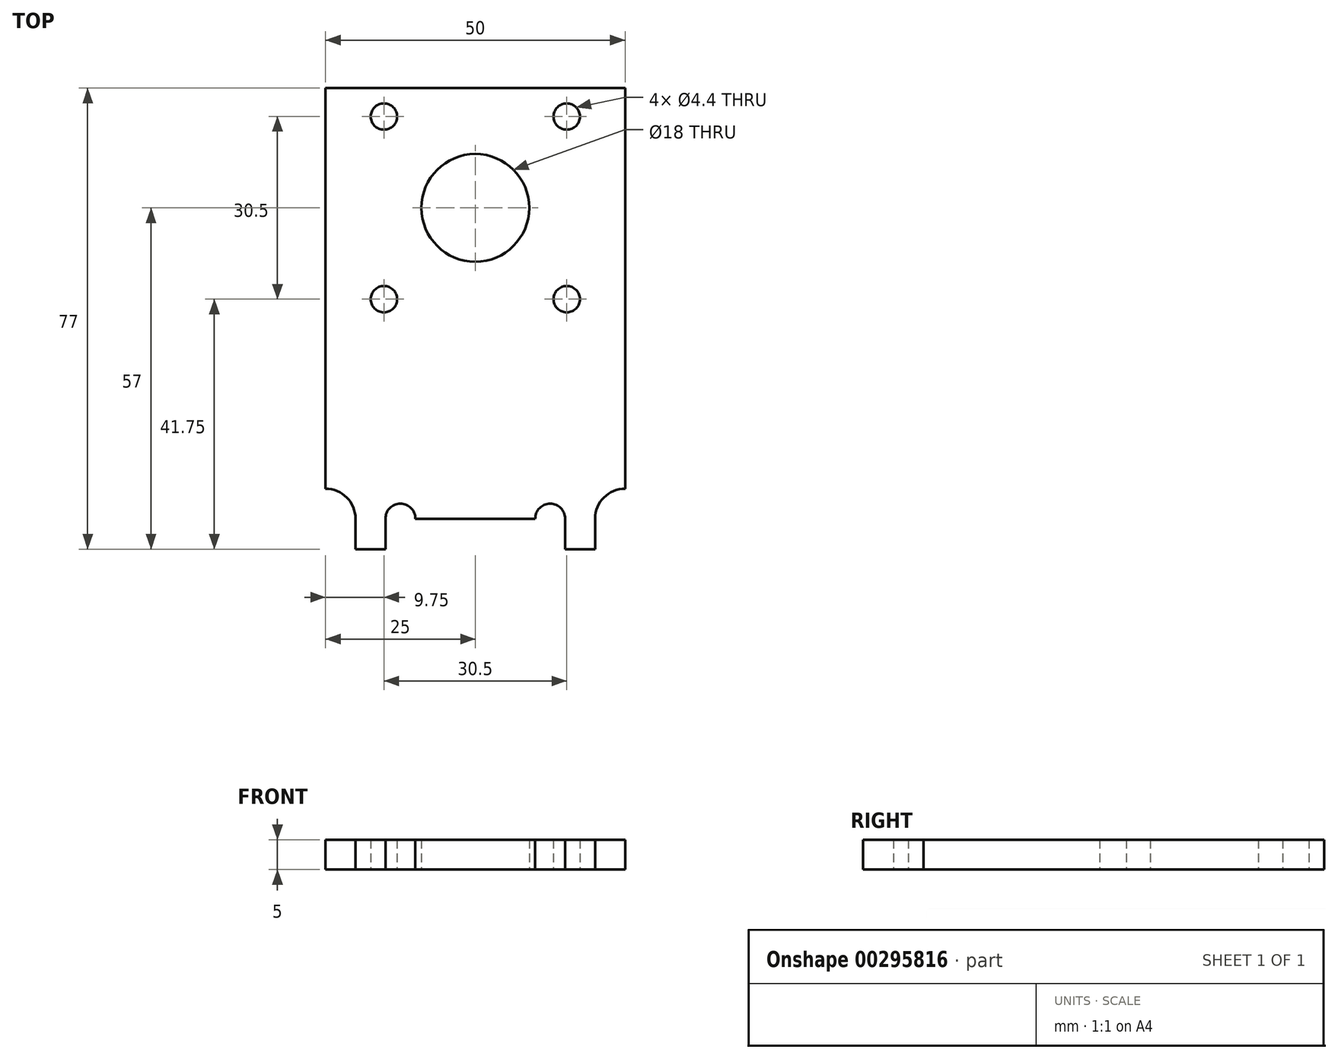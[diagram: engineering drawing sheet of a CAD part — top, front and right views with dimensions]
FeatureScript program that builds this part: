
annotation { "Feature Type Name" : "Feature", "Feature Type Description" : "" }
export const myFeature = defineFeature(function(context is Context, id is Id, definition is map)
    precondition{}
    {
        {
            assignVariable(context, id + "F0", {"name" : "AlThickness", "anyValue" : 5 * mm});
        }
        {
            var Q0;
            Q0=qCreatedBy(makeId("Top.planeOp"),FACE);
            var sketch = newSketch(context, id + "F1", { "sketchPlane" : qUnion([Q0])});
            skLineSegment(sketch, "E0.bottom", {"start": v(20, -20) * mm, "end": v(-20, -20) * mm, "construction": true});
            skLineSegment(sketch, "E0.top", {"start": v(20, 20) * mm, "end": v(-20, 20) * mm});
            skPoint(sketch, "E0.middle", {"position": v(0, 0) * mm});
            skCircle(sketch, "E1", {"center": v(0, 0) * mm, "radius": 9 * mm});
            skLineSegment(sketch, "E2", {"start": v(0, 0) * mm, "end": v(0, -20) * mm, "construction": true});
            skPoint(sketch, "E3.endSnap0", {"position": v(0, 20) * mm});
            skLineSegment(sketch, "E4", {"start": v(0, 0) * mm, "end": v(0, 20) * mm, "construction": true});
            skLineSegment(sketch, "E5.left", {"start": v(-15, -57) * mm, "end": v(-15, -51.9) * mm});
            skLineSegment(sketch, "E5.right", {"start": v(15, -57) * mm, "end": v(15, -51.9) * mm});
            skCircle(sketch, "E6", {"center": v(-15.25, 15.25) * mm, "radius": 2.2 * mm});
            skCircle(sketch, "E7.MirrorC", {"center": v(15.25, 15.25) * mm, "radius": 2.2 * mm});
            skCircle(sketch, "E8.MirrorC", {"center": v(-15.25, -15.25) * mm, "radius": 2.2 * mm});
            skCircle(sketch, "E9.MirrorC", {"center": v(15.25, -15.25) * mm, "radius": 2.2 * mm});
            skArc(sketch, "E10", {"start": v(-10, -51.9) * mm, "mid": v(-12.5, -49.4) * mm, "end": v(-15, -51.9) * mm});
            skArc(sketch, "E11.MirrorCS", {"start": v(10, -51.9) * mm, "mid": v(12.5, -49.4) * mm, "end": v(15, -51.9) * mm});
            skLineSegment(sketch, "E12", {"start": v(-10, -51.9) * mm, "end": v(0, -51.9) * mm});
            skLineSegment(sketch, "E13", {"start": v(10, -51.9) * mm, "end": v(0, -51.9) * mm});
            skLineSegment(sketch, "E14", {"start": v(-20, -57) * mm, "end": v(-15, -57) * mm});
            skLineSegment(sketch, "E15", {"start": v(15, -57) * mm, "end": v(20, -57) * mm});
            skLineSegment(sketch, "E16.bottom", {"start": v(20, 20) * mm, "end": v(20, 20) * mm});
            skLineSegment(sketch, "E16.top", {"start": v(20, -57) * mm, "end": v(20, -57) * mm});
            skLineSegment(sketch, "E16.left", {"start": v(20, -51.9) * mm, "end": v(20, -57) * mm});
            skLineSegment(sketch, "E17.left", {"start": v(20, -57) * mm, "end": v(20, -51.9) * mm});
            skLineSegment(sketch, "E18", {"start": v(15, -51.9) * mm, "end": v(20, -51.9) * mm, "construction": true});
            skLineSegment(sketch, "E19.top", {"start": v(20, 20) * mm, "end": v(25, 20) * mm});
            skLineSegment(sketch, "E19.right", {"start": v(25, -46.9) * mm, "end": v(25, 20) * mm});
            skArc(sketch, "E20", {"start": v(25, -46.9) * mm, "mid": v(21.46, -48.36) * mm, "end": v(20, -51.9) * mm});
            skLineSegment(sketch, "E21.MirrorCS", {"start": v(-25, -46.9) * mm, "end": v(-25, 20) * mm});
            skLineSegment(sketch, "E22.MirrorCS", {"start": v(-20, 20) * mm, "end": v(-25, 20) * mm});
            skArc(sketch, "E23.MirrorCS", {"start": v(-25, -46.9) * mm, "mid": v(-21.46, -48.36) * mm, "end": v(-20, -51.9) * mm});
            skLineSegment(sketch, "E24.trimOffspring", {"start": v(-20, -51.9) * mm, "end": v(-20, -57) * mm});
            skPoint(sketch, "E25.MirrorCS.start.orphan", {"position": v(-20, 20) * mm});
            skLineSegment(sketch, "E26", {"start": v(-20, -20) * mm, "end": v(-20, -51.9) * mm, "construction": true});
            skLineSegment(sketch, "E27", {"start": v(20, -20) * mm, "end": v(20, -51.9) * mm, "construction": true});
            skSolve(sketch);
        }
        {
            var Q0;
            Q0=makeQuery(id+"F1.imprint","IMPRINT",FACE,{"disambiguationData":[TD([[makeQuery(id+"F1.imprint","IMPRINT",EDGE,{"derivedFrom":sQuery(id+"F1.wireOp",EDGE,"E0.top")}),1.0]])]});
            var Q1;
            Q1=makeQuery(id+"F1.imprint","IMPRINT",FACE,{"disambiguationData":[TD([[makeQuery(id+"F1.imprint","IMPRINT",EDGE,{"derivedFrom":sQuery(id+"F1.wireOp",EDGE,"YBB4CGkO-1guZ-VOgm-T3uK-C8Wn4KZtJpau.bottom")}),-1.0]])]});
            extrude(context, id + "F2", {"entities" : qUnion([Q0, Q1]), "depth" : getVariable(context, 'AlThickness')});
        }
    });
